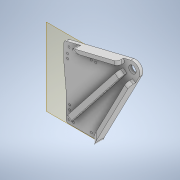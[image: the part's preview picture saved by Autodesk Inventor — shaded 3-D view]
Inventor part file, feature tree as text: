
AUTODESK INVENTOR PART (.ipt)
format: ipt  version: 2022 (Build 260153000, 153)  size: 424,960 bytes
history: native  units: mm
features: other x5, extrude x2, sketch x2, fillet x1, reference x1
ambient origin geometry x8: Origin, YZ Plane, XZ Plane, XY Plane, X Axis, Y Axis, Z Axis, Center Point
bodies: Body1 (feature_tree)
feature tree (11):
  other  "Твердое тело1"
  other  "РабПлоскость1"
  extrude  "Выдавливание1"  Depth=2.5mm TaperAngle=0.0deg
  extrude  "Выдавливание2"  Depth=6.0mm
  fillet  "Сопряжение1"  Radius=12.0mm
  sketch  "Эскиз1"
  reference  "Ссылка1"
  sketch  "Эскиз5"
  other  "<userpath>\Documents\Inventor\AIM\Aim.iam"
  other  "Aim.iam"
  other  "Base:2"
